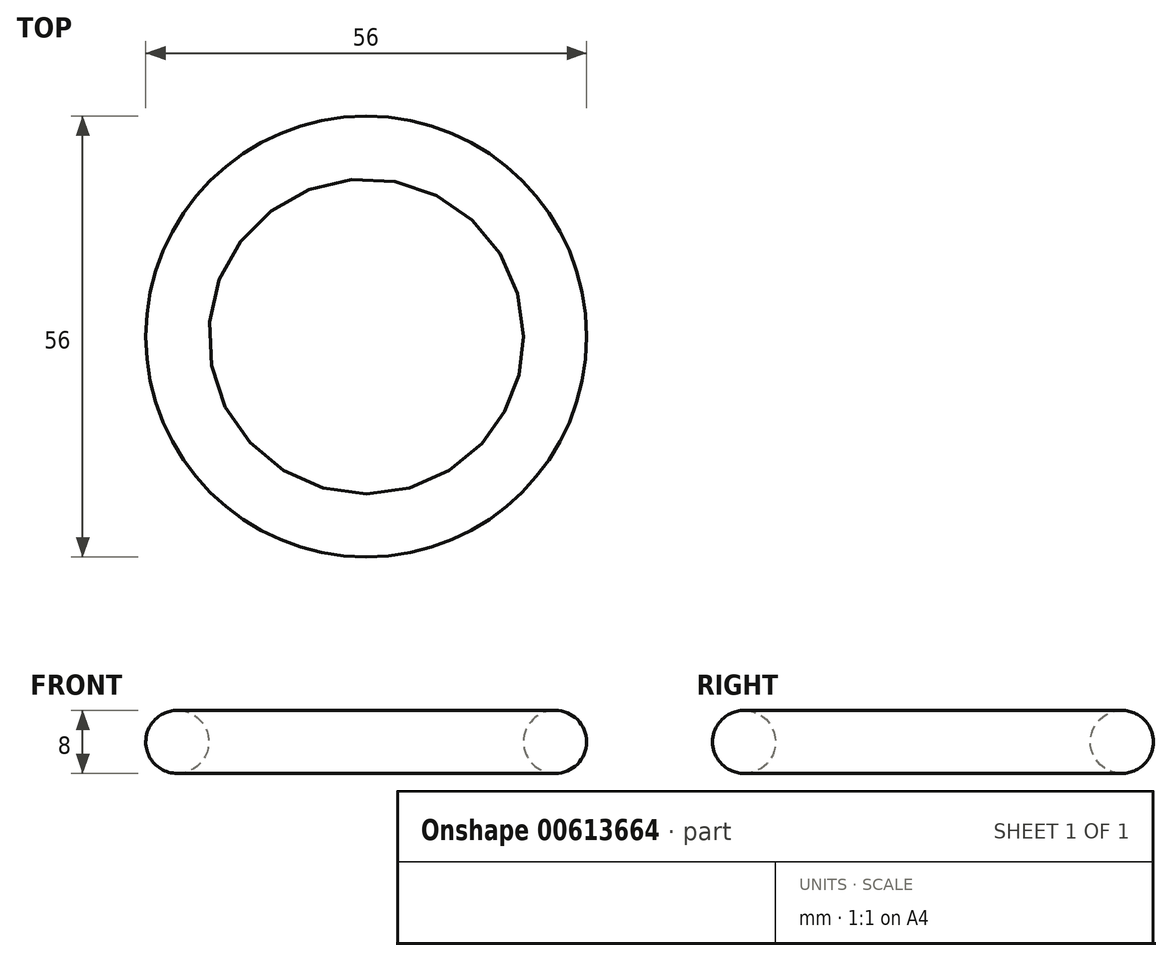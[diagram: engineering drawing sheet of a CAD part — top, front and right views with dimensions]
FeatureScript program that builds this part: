
annotation { "Feature Type Name" : "Feature", "Feature Type Description" : "" }
export const myFeature = defineFeature(function(context is Context, id is Id, definition is map)
    precondition{}
    {
        {
            var Q0;
            Q0=qCreatedBy(makeId("Front.planeOp"),FACE);
            var sketch = newSketch(context, id + "F0", { "sketchPlane" : qUnion([Q0])});
            skLineSegment(sketch, "E0", {"start": v(0, 42.2) * mm, "end": v(0, -44.71) * mm});
            skLineSegment(sketch, "E1", {"start": v(0, 0) * mm, "end": v(20, 0) * mm});
            skLineSegment(sketch, "E2", {"start": v(20, 0) * mm, "end": v(24, 0) * mm});
            skCircle(sketch, "E3", {"center": v(24, 0) * mm, "radius": 4 * mm});
            skSolve(sketch);
        }
        {
            var Q0;
            Q0 = qSketchRegion(id + "F0", true);
            var Q1;
            Q1=sQuery(id+"F0.wireOp",EDGE,"E0");
            revolve(context, id + "F1", {"entities" : qUnion([Q0]), "axis" : qUnion([Q1]), "revolveType" : RevolveType.FULL});
        }
    });
